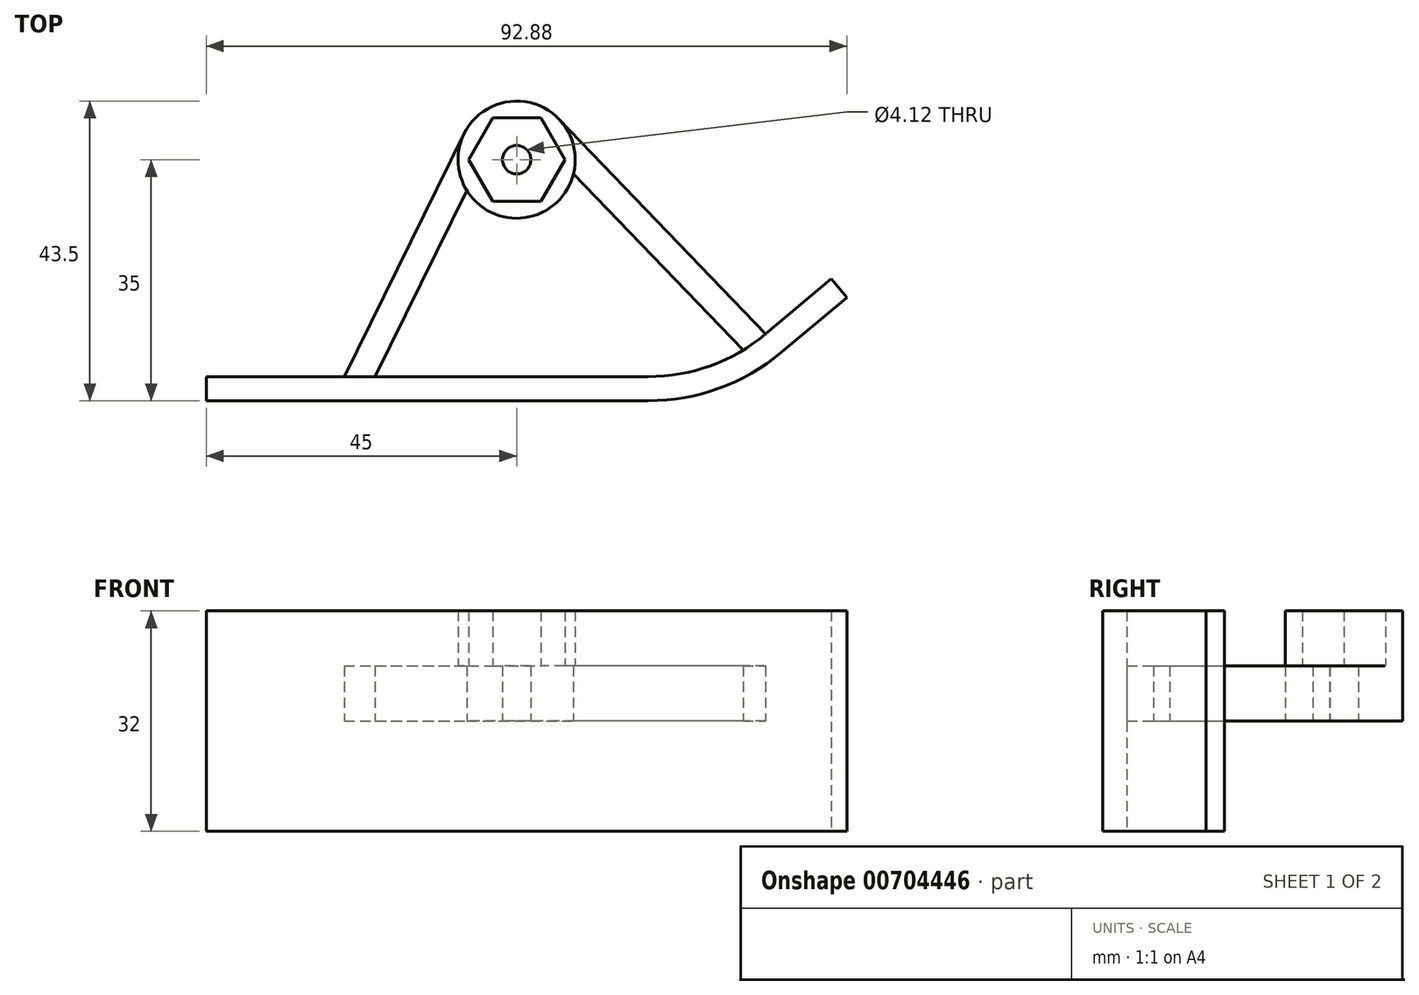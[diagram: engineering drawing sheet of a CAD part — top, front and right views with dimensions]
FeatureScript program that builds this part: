
annotation { "Feature Type Name" : "Feature", "Feature Type Description" : "" }
export const myFeature = defineFeature(function(context is Context, id is Id, definition is map)
    precondition{}
    {
        {
            var Q0;
            Q0=qCreatedBy(makeId("Top.planeOp"),FACE);
            var sketch = newSketch(context, id + "F0", { "sketchPlane" : qUnion([Q0])});
            skLineSegment(sketch, "E0", {"start": v(-45, 0) * mm, "end": v(19.08, 0) * mm});
            skLineSegment(sketch, "E1", {"start": v(38.36, 7.02) * mm, "end": v(47.88, 15) * mm});
            skPoint(sketch, "E2.visualSharp", {"position": v(30, 0) * mm});
            skArc(sketch, "E2.filletArc", {"start": v(19.08, 0) * mm, "mid": v(29.34, 1.8) * mm, "end": v(38.36, 7.02) * mm});
            skLineSegment(sketch, "E3.0", {"start": v(36.11, 9.7) * mm, "end": v(45.63, 17.68) * mm});
            skArc(sketch, "E3.1", {"start": v(19.08, 3.5) * mm, "mid": v(28.14, 5.1) * mm, "end": v(36.11, 9.7) * mm});
            skLineSegment(sketch, "E3.2", {"start": v(-45, 3.5) * mm, "end": v(19.08, 3.5) * mm});
            skLineSegment(sketch, "E4", {"start": v(47.88, 15) * mm, "end": v(45.63, 17.68) * mm});
            skLineSegment(sketch, "E5", {"start": v(-45, 3.5) * mm, "end": v(-45, 0) * mm});
            skSolve(sketch);
        }
        {
            var Q0;
            Q0=makeQuery(id+"F0.imprint","IMPRINT",FACE,{"disambiguationData":[TD([[makeQuery(id+"F0.imprint","IMPRINT",EDGE,{"derivedFrom":sQuery(id+"F0.wireOp",EDGE,"E0")}),1.0]])]});
            extrude(context, id + "F1", {"entities" : qUnion([Q0]), "depth" : 32 * mm, "offsetDistance" : 25 * mm, "symmetric" : true});
        }
        {
            var Q0;
            Q0=qCreatedBy(makeId("Top.planeOp"),FACE);
            var sketch = newSketch(context, id + "F2", { "sketchPlane" : qUnion([Q0])});
            skCircle(sketch, "E6", {"center": v(0, 35) * mm, "radius": 8.5 * mm, "construction": true});
            skLineSegment(sketch, "E7.0", {"start": v(-45, 3.5) * mm, "end": v(19.08, 3.5) * mm});
            skArc(sketch, "E8.0", {"start": v(19.08, 3.5) * mm, "mid": v(28.14, 5.1) * mm, "end": v(36.11, 9.7) * mm});
            skLineSegment(sketch, "E9.0", {"start": v(36.11, 9.7) * mm, "end": v(45.63, 17.68) * mm});
            skLineSegment(sketch, "E10", {"start": v(36.11, 9.7) * mm, "end": v(6.13, 40.9) * mm});
            skLineSegment(sketch, "E11", {"start": v(-25, 3.5) * mm, "end": v(-7.62, 38.76) * mm});
            skLineSegment(sketch, "E12", {"start": v(45.63, 17.68) * mm, "end": v(36.11, 9.7) * mm});
            skLineSegment(sketch, "E13.0", {"start": v(-20.54, 3.5) * mm, "end": v(-7.22, 30.52) * mm});
            skLineSegment(sketch, "E14.0", {"start": v(32.83, 7.35) * mm, "end": v(8.24, 32.92) * mm});
            skCircle(sketch, "E15", {"center": v(0, 35) * mm, "radius": 8.5 * mm});
            skCircle(sketch, "E16", {"center": v(0, 35) * mm, "radius": 2.06 * mm});
            skSolve(sketch);
        }
        {
            var Q0;
            {var subQ2=sQuery(id+"F2.wireOp",EDGE,"E11");Q0=makeQuery(id+"F2.imprint","IMPRINT",FACE,{"disambiguationData":[TD([[makeQuery(id+"F2.imprint","IMPRINT",EDGE,{"derivedFrom":subQ2}),-1.0]])]});}
            var Q1;
            Q1=makeQuery(id+"F2.imprint","IMPRINT",FACE,{"disambiguationData":[TD([[makeQuery(id+"F2.imprint","IMPRINT",EDGE,{"derivedFrom":sQuery(id+"F2.wireOp",EDGE,"E16")}),-1.0]])]});
            var Q2;
            {var subQ1=sQuery(id+"F2.wireOp",EDGE,"E10");Q2=makeQuery(id+"F2.imprint","IMPRINT",FACE,{"disambiguationData":[TD([[makeQuery(id+"F2.imprint","IMPRINT",EDGE,{"derivedFrom":subQ1}),1.0]])]});}
            extrude(context, id + "F3", {"entities" : qUnion([Q0, Q1, Q2]), "operationType" : NewBodyOperationType.ADD, "depth" : 8 * mm, "offsetDistance" : 25 * mm});
        }
        {
            var Q0;
            Q0=makeQuery(id+"F3.opExtrude","CAP_FACE",FACE,{"disambiguationData":[OSD([sQuery(id+"F2.wireOp",EDGE,"E7.0"),sQuery(id+"F2.wireOp",EDGE,"E8.0"),sQuery(id+"F2.wireOp",EDGE,"E10"),sQuery(id+"F2.wireOp",EDGE,"E11"),sQuery(id+"F2.wireOp",EDGE,"E13.0"),sQuery(id+"F2.wireOp",EDGE,"E14.0"),sQuery(id+"F2.wireOp",EDGE,"E15"),sQuery(id+"F2.wireOp",EDGE,"E16")])],"isStart":false});
            var sketch = newSketch(context, id + "F4", { "sketchPlane" : qUnion([Q0])});
            skCircle(sketch, "E17.cCircle", {"center": v(0, 35) * mm, "radius": 6.05 * mm, "construction": true});
            skLineSegment(sketch, "E17.0", {"start": v(-3.5, 41.05) * mm, "end": v(3.5, 41.05) * mm});
            skLineSegment(sketch, "E17.1", {"start": v(3.5, 41.05) * mm, "end": v(6.99, 35) * mm});
            skLineSegment(sketch, "E17.2", {"start": v(6.99, 35) * mm, "end": v(3.5, 28.95) * mm});
            skLineSegment(sketch, "E17.3", {"start": v(3.5, 28.95) * mm, "end": v(-3.5, 28.95) * mm});
            skLineSegment(sketch, "E17.4", {"start": v(-3.5, 28.95) * mm, "end": v(-6.99, 35) * mm});
            skLineSegment(sketch, "E17.5", {"start": v(-6.99, 35) * mm, "end": v(-3.5, 41.05) * mm});
            skPoint(sketch, "E17.0.midPoint", {"position": v(0, 41.05) * mm});
            skCircle(sketch, "E18", {"center": v(0, 35) * mm, "radius": 8.5 * mm});
            skSolve(sketch);
        }
        {
            var Q0;
            Q0=makeQuery(id+"F4.imprint","IMPRINT",FACE,{"disambiguationData":[TD([[makeQuery(id+"F4.imprint","IMPRINT",EDGE,{"derivedFrom":sQuery(id+"F4.wireOp",EDGE,"E17.0")}),1.0]])]});
            extrude(context, id + "F5", {"entities" : qUnion([Q0]), "operationType" : NewBodyOperationType.ADD, "depth" : 8 * mm, "offsetDistance" : 25 * mm});
        }
    });
